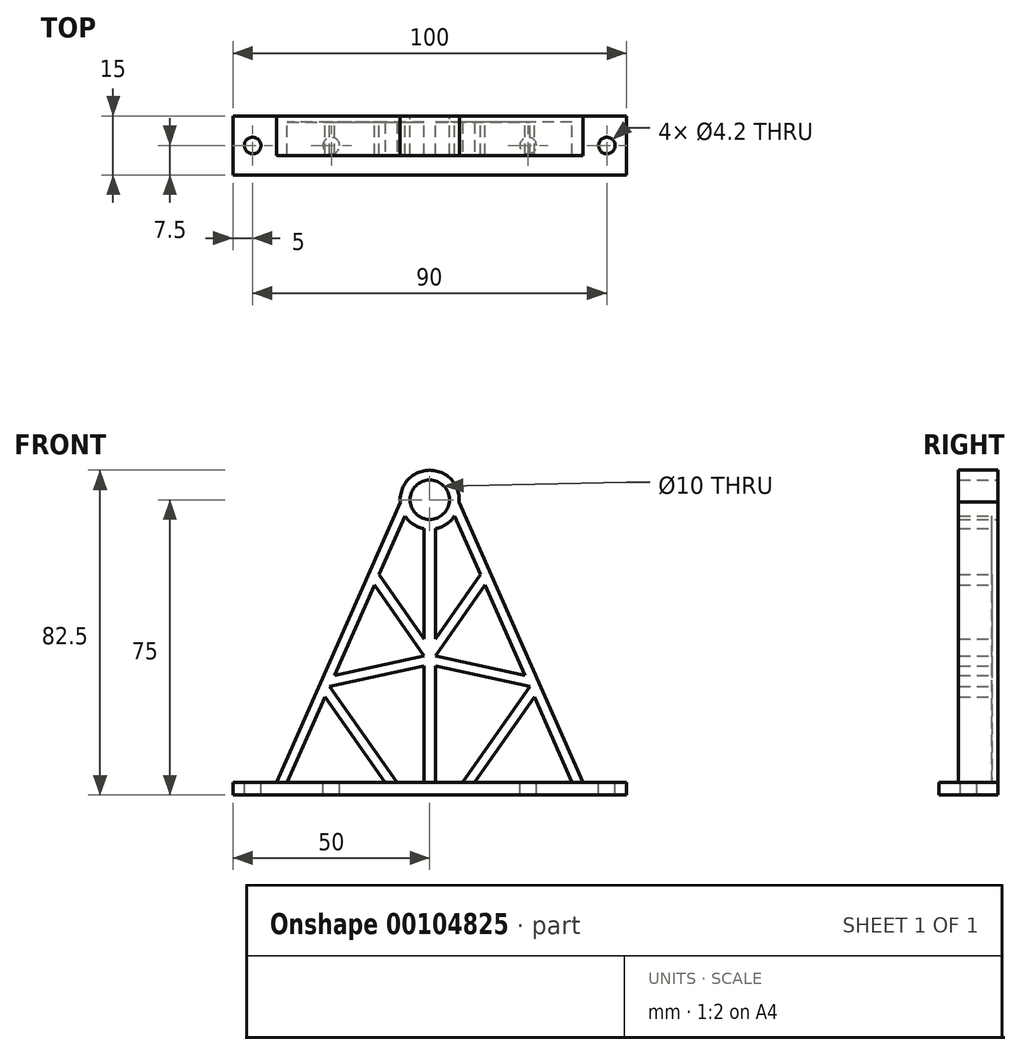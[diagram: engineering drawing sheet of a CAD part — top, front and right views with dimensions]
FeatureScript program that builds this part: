
annotation { "Feature Type Name" : "Feature", "Feature Type Description" : "" }
export const myFeature = defineFeature(function(context is Context, id is Id, definition is map)
    precondition{}
    {
        {
            var Q0;
            Q0=qCreatedBy(makeId("Front.planeOp"),FACE);
            var sketch = newSketch(context, id + "F0", { "sketchPlane" : qUnion([Q0])});
            skArc(sketch, "E0", {"start": v(0, 70) * mm, "mid": v(5, 75) * mm, "end": v(0, 80) * mm});
            skArc(sketch, "E1", {"start": v(1.5, 67.65) * mm, "mid": v(4.23, 68.8) * mm, "end": v(6.3, 70.94) * mm});
            skLineSegment(sketch, "E2.bottom", {"start": v(0, 0) * mm, "end": v(40, 0) * mm});
            skLineSegment(sketch, "E2.top", {"start": v(1.5, 3) * mm, "end": v(8.22, 3) * mm});
            skLineSegment(sketch, "E2.right", {"start": v(40, 0) * mm, "end": v(39, 3) * mm});
            skLineSegment(sketch, "E3", {"start": v(0, 0) * mm, "end": v(0, 102.89) * mm, "construction": true});
            skLineSegment(sketch, "E4", {"start": v(1.5, 3) * mm, "end": v(1.5, 32.77) * mm});
            skLineSegment(sketch, "E5", {"start": v(7.48, 74.46) * mm, "end": v(39, 3) * mm});
            skPoint(sketch, "E5.startSnap0", {"position": v(7.48, 75.54) * mm});
            skLineSegment(sketch, "E6", {"start": v(36.27, 3) * mm, "end": v(26.6, 24.9) * mm});
            skArc(sketch, "E7.trimOffspring", {"start": v(7.48, 74.46) * mm, "mid": v(5.49, 80.1) * mm, "end": v(0, 82.5) * mm});
            skLineSegment(sketch, "E8", {"start": v(26.6, 24.9) * mm, "end": v(11.27, 3) * mm});
            skLineSegment(sketch, "E9", {"start": v(25.43, 27.58) * mm, "end": v(8.22, 3) * mm});
            skLineSegment(sketch, "E10", {"start": v(12.9, 55.97) * mm, "end": v(1.5, 39.68) * mm});
            skLineSegment(sketch, "E11", {"start": v(14.08, 53.3) * mm, "end": v(1.5, 35.33) * mm});
            skLineSegment(sketch, "E12.trimOffspring", {"start": v(1.5, 39.68) * mm, "end": v(1.5, 67.65) * mm});
            skLineSegment(sketch, "E13.trimOffspring", {"start": v(12.9, 55.97) * mm, "end": v(6.3, 70.94) * mm});
            skLineSegment(sketch, "E14.trimOffspring", {"start": v(24.18, 30.4) * mm, "end": v(14.08, 53.3) * mm});
            skLineSegment(sketch, "E15.trimOffspring", {"start": v(11.27, 3) * mm, "end": v(36.27, 3) * mm});
            skLineSegment(sketch, "E16", {"start": v(1.5, 35.33) * mm, "end": v(24.18, 30.4) * mm});
            skLineSegment(sketch, "E17", {"start": v(1.5, 32.77) * mm, "end": v(25.43, 27.58) * mm});
            skLineSegment(sketch, "E18.MirrorCS", {"start": v(-40, 0) * mm, "end": v(-39, 3) * mm});
            skLineSegment(sketch, "E19.MirrorCS", {"start": v(-12.9, 55.97) * mm, "end": v(-1.5, 39.68) * mm});
            skLineSegment(sketch, "E20.MirrorCS", {"start": v(-25.43, 27.58) * mm, "end": v(-8.22, 3) * mm});
            skLineSegment(sketch, "E21.MirrorCS", {"start": v(-26.6, 24.9) * mm, "end": v(-11.27, 3) * mm});
            skLineSegment(sketch, "E22.MirrorCS", {"start": v(-1.5, 35.33) * mm, "end": v(-24.18, 30.4) * mm});
            skLineSegment(sketch, "E23.MirrorCS", {"start": v(-24.18, 30.4) * mm, "end": v(-14.08, 53.3) * mm});
            skLineSegment(sketch, "E24.MirrorCS", {"start": v(-1.5, 32.77) * mm, "end": v(-25.43, 27.58) * mm});
            skLineSegment(sketch, "E25.MirrorCS", {"start": v(-1.5, 39.68) * mm, "end": v(-1.5, 67.65) * mm});
            skLineSegment(sketch, "E26.MirrorCS", {"start": v(-11.27, 3) * mm, "end": v(-36.27, 3) * mm});
            skLineSegment(sketch, "E27.MirrorCS", {"start": v(-12.9, 55.97) * mm, "end": v(-6.3, 70.94) * mm});
            skLineSegment(sketch, "E28.MirrorCS", {"start": v(-14.08, 53.3) * mm, "end": v(-1.5, 35.33) * mm});
            skArc(sketch, "E29.MirrorCS", {"start": v(-7.48, 74.46) * mm, "mid": v(-5.49, 80.1) * mm, "end": v(0, 82.5) * mm});
            skLineSegment(sketch, "E30.MirrorCS", {"start": v(-36.27, 3) * mm, "end": v(-26.6, 24.9) * mm});
            skLineSegment(sketch, "E31.MirrorCS", {"start": v(-7.48, 74.46) * mm, "end": v(-39, 3) * mm});
            skArc(sketch, "E32.MirrorCS", {"start": v(0, 70) * mm, "mid": v(-5, 75) * mm, "end": v(0, 80) * mm});
            skArc(sketch, "E33.MirrorCS", {"start": v(-1.5, 67.65) * mm, "mid": v(-4.23, 68.8) * mm, "end": v(-6.3, 70.94) * mm});
            skPoint(sketch, "E34.MirrorP", {"position": v(-7.48, 75.54) * mm});
            skLineSegment(sketch, "E35.MirrorCS", {"start": v(0, 0) * mm, "end": v(-40, 0) * mm});
            skLineSegment(sketch, "E36.MirrorCS", {"start": v(-1.5, 3) * mm, "end": v(-8.22, 3) * mm});
            skLineSegment(sketch, "E37.MirrorCS", {"start": v(-1.5, 3) * mm, "end": v(-1.5, 32.77) * mm});
            skSolve(sketch);
        }
        {
            var Q0;
            Q0 = qSketchRegion(id + "F0", true);
            extrude(context, id + "F1", {"entities" : qUnion([Q0]), "depth" : 10 * mm});
        }
        {
            var Q0;
            Q0=makeQuery(id+"F1.opExtrude","CAP_FACE",FACE,{"disambiguationData":[OSD([sQuery(id+"F0.wireOp",EDGE,"E0"),sQuery(id+"F0.wireOp",EDGE,"E1"),sQuery(id+"F0.wireOp",EDGE,"E2.bottom"),sQuery(id+"F0.wireOp",EDGE,"E2.top"),sQuery(id+"F0.wireOp",EDGE,"E2.right"),sQuery(id+"F0.wireOp",EDGE,"E4"),sQuery(id+"F0.wireOp",EDGE,"E5"),sQuery(id+"F0.wireOp",EDGE,"E6"),sQuery(id+"F0.wireOp",EDGE,"E7.trimOffspring"),sQuery(id+"F0.wireOp",EDGE,"E8"),sQuery(id+"F0.wireOp",EDGE,"E9"),sQuery(id+"F0.wireOp",EDGE,"E10"),sQuery(id+"F0.wireOp",EDGE,"E11"),sQuery(id+"F0.wireOp",EDGE,"E12.trimOffspring"),sQuery(id+"F0.wireOp",EDGE,"E13.trimOffspring"),sQuery(id+"F0.wireOp",EDGE,"E14.trimOffspring"),sQuery(id+"F0.wireOp",EDGE,"E15.trimOffspring"),sQuery(id+"F0.wireOp",EDGE,"E16"),sQuery(id+"F0.wireOp",EDGE,"E17"),sQuery(id+"F0.wireOp",EDGE,"E18.MirrorCS"),sQuery(id+"F0.wireOp",EDGE,"E19.MirrorCS"),sQuery(id+"F0.wireOp",EDGE,"E20.MirrorCS"),sQuery(id+"F0.wireOp",EDGE,"E21.MirrorCS"),sQuery(id+"F0.wireOp",EDGE,"E22.MirrorCS"),sQuery(id+"F0.wireOp",EDGE,"E23.MirrorCS"),sQuery(id+"F0.wireOp",EDGE,"E24.MirrorCS"),sQuery(id+"F0.wireOp",EDGE,"E25.MirrorCS"),sQuery(id+"F0.wireOp",EDGE,"E26.MirrorCS"),sQuery(id+"F0.wireOp",EDGE,"E27.MirrorCS"),sQuery(id+"F0.wireOp",EDGE,"E28.MirrorCS"),sQuery(id+"F0.wireOp",EDGE,"E29.MirrorCS"),sQuery(id+"F0.wireOp",EDGE,"E30.MirrorCS"),sQuery(id+"F0.wireOp",EDGE,"E31.MirrorCS"),sQuery(id+"F0.wireOp",EDGE,"E32.MirrorCS"),sQuery(id+"F0.wireOp",EDGE,"E33.MirrorCS"),sQuery(id+"F0.wireOp",EDGE,"E35.MirrorCS"),sQuery(id+"F0.wireOp",EDGE,"E36.MirrorCS"),sQuery(id+"F0.wireOp",EDGE,"E37.MirrorCS")])],"isStart":false});
            var sketch = newSketch(context, id + "F2", { "sketchPlane" : qUnion([Q0])});
            skLineSegment(sketch, "E38", {"start": v(-7.48, 74.46) * mm, "end": v(-1.5, 67.65) * mm});
            skLineSegment(sketch, "E39", {"start": v(-1.5, 67.65) * mm, "end": v(1.5, 67.65) * mm});
            skLineSegment(sketch, "E40", {"start": v(1.5, 67.65) * mm, "end": v(7.48, 74.46) * mm});
            skLineSegment(sketch, "E41", {"start": v(7.48, 74.46) * mm, "end": v(40, 0) * mm});
            skLineSegment(sketch, "E42", {"start": v(40, 0) * mm, "end": v(-40, 0) * mm});
            skLineSegment(sketch, "E43", {"start": v(-40, 0) * mm, "end": v(-7.48, 74.46) * mm});
            skSolve(sketch);
        }
        {
            var Q0;
            Q0 = qSketchRegion(id + "F2", true);
            extrude(context, id + "F3", {"entities" : qUnion([Q0]), "operationType" : NewBodyOperationType.ADD, "oppositeDirection" : true, "depth" : 10 * mm, "hasSecondDirection" : true, "secondDirectionOppositeDirection" : true, "secondDirectionDepth" : 8.5 * mm});
        }
        {
            var Q0;
            Q0=qCreatedBy(makeId("Front.planeOp"),FACE);
            var sketch = newSketch(context, id + "F4", { "sketchPlane" : qUnion([Q0])});
            skLineSegment(sketch, "E44.bottom", {"start": v(-50, 0) * mm, "end": v(50, 0) * mm});
            skLineSegment(sketch, "E44.top", {"start": v(-50, 3.16) * mm, "end": v(50, 3.16) * mm});
            skLineSegment(sketch, "E44.left", {"start": v(-50, 0) * mm, "end": v(-50, 3.16) * mm});
            skLineSegment(sketch, "E44.right", {"start": v(50, 0) * mm, "end": v(50, 3.16) * mm});
            skSolve(sketch);
        }
        {
            var Q0;
            Q0 = qSketchRegion(id + "F4", true);
            extrude(context, id + "F5", {"entities" : qUnion([Q0]), "operationType" : NewBodyOperationType.ADD, "depth" : 15 * mm});
        }
        {
            var Q0;
            Q0=makeQuery(id+"F5.opExtrude","SWEPT_FACE",FACE,{"disambiguationData":[OSD([sQuery(id+"F4.wireOp",EDGE,"E44.top")])]});
            var sketch = newSketch(context, id + "F6", { "sketchPlane" : qUnion([Q0])});
            skLineSegment(sketch, "E45", {"start": v(-50, -7.5) * mm, "end": v(50, -7.5) * mm, "construction": true});
            skCircle(sketch, "E46", {"center": v(-45, -7.5) * mm, "radius": 2.1 * mm});
            skCircle(sketch, "E47", {"center": v(45, -7.5) * mm, "radius": 2.1 * mm});
            skCircle(sketch, "E48", {"center": v(-25, -7.5) * mm, "radius": 2.1 * mm});
            skCircle(sketch, "E49", {"center": v(25, -7.5) * mm, "radius": 2.1 * mm});
            skSolve(sketch);
        }
        {
            var Q0;
            Q0 = qSketchRegion(id + "F6", true);
            extrude(context, id + "F7", {"entities" : qUnion([Q0]), "operationType" : NewBodyOperationType.REMOVE, "endBound" : BoundingType.UP_TO_NEXT, "oppositeDirection" : true, "depth" : 25 * mm});
        }
    });
